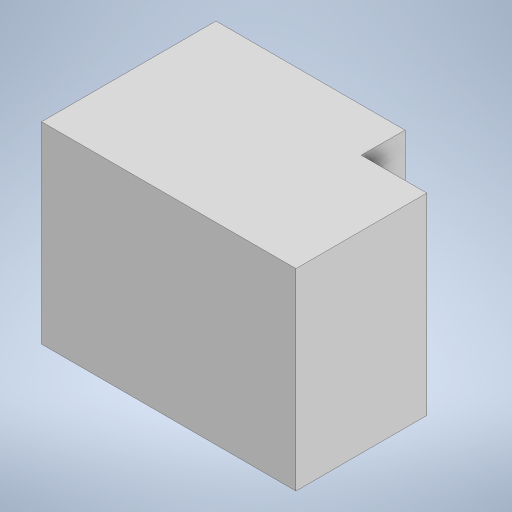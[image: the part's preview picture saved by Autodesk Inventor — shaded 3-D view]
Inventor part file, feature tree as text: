
AUTODESK INVENTOR PART (.ipt)
format: ipt  version: 2023 (Build 270158000, 158)  size: 167,936 bytes
history: native  units: mm
features: extrude x1, sketch x1
ambient origin geometry x8: Origin, YZ Plane, XZ Plane, XY Plane, X Axis, Y Axis, Z Axis, Center Point
bodies: 实体1 (feature_tree)
feature tree (2):
  extrude  "拉伸1"  Depth=3500.0mm
  sketch  "草图1"  dims[d0=2400.0mm d1=3500.0mm d2=1800.0mm d3=900.0mm d4=2650.0mm d5=0.0mm]
